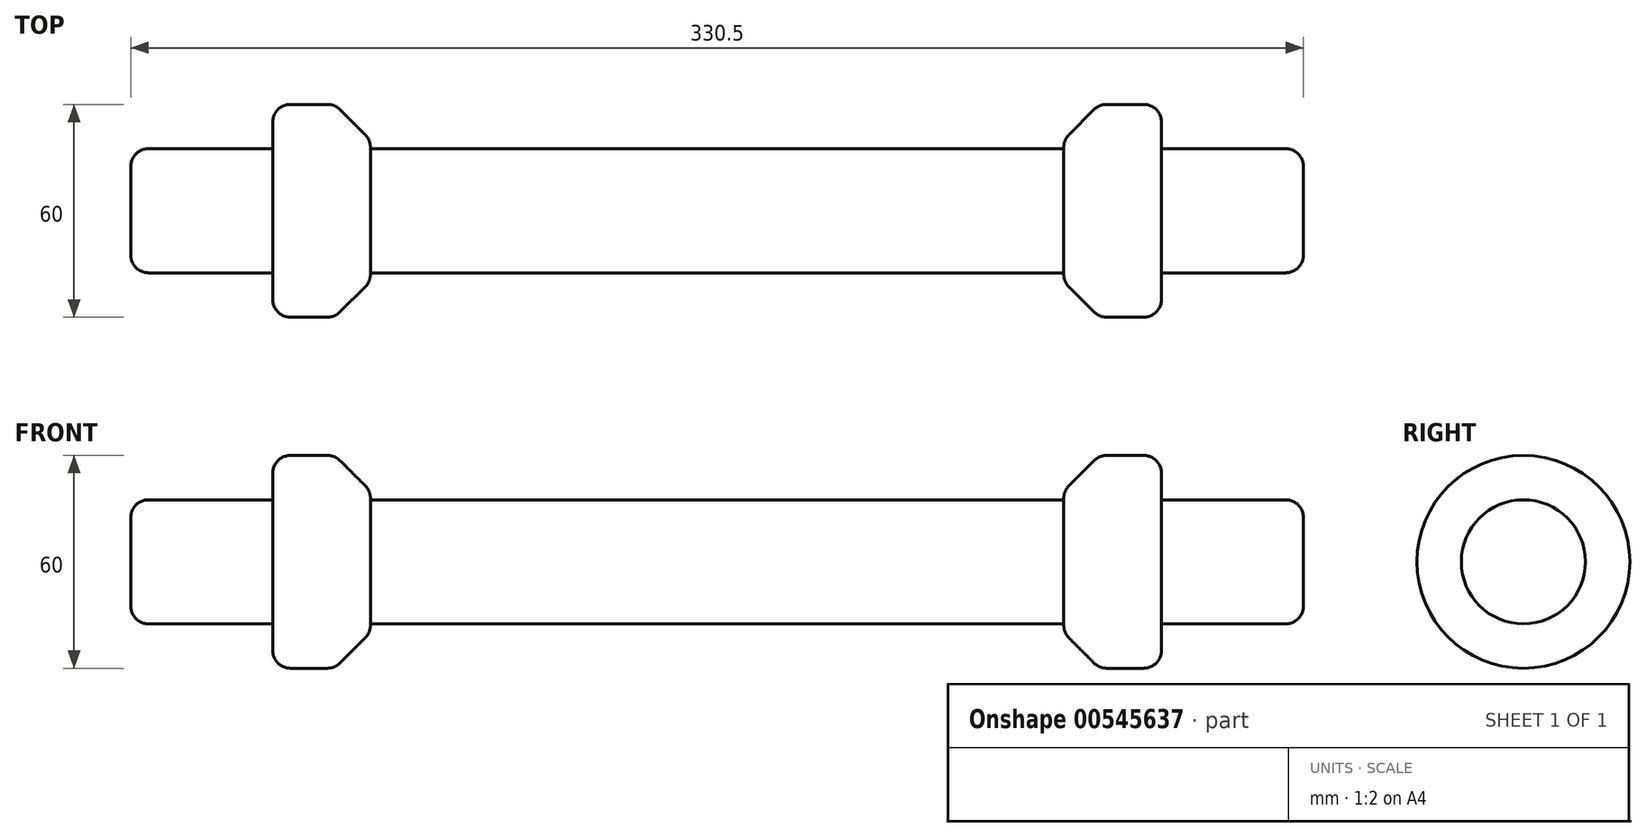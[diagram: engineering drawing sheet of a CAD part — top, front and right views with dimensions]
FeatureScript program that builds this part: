
annotation { "Feature Type Name" : "Feature", "Feature Type Description" : "" }
export const myFeature = defineFeature(function(context is Context, id is Id, definition is map)
    precondition{}
    {
        {
            var Q0;
            Q0=qCreatedBy(makeId("Front.planeOp"),FACE);
            var sketch = newSketch(context, id + "F0", { "sketchPlane" : qUnion([Q0])});
            skLineSegment(sketch, "E0", {"start": v(0, 0) * mm, "end": v(165.25, 0) * mm});
            skLineSegment(sketch, "E1", {"start": v(165.25, 0) * mm, "end": v(165.25, 17.5) * mm});
            skLineSegment(sketch, "E2", {"start": v(165.25, 17.5) * mm, "end": v(125.25, 17.5) * mm});
            skLineSegment(sketch, "E3", {"start": v(125.25, 17.5) * mm, "end": v(125.25, 30) * mm});
            skLineSegment(sketch, "E4", {"start": v(125.25, 30) * mm, "end": v(97.7, 30) * mm});
            skLineSegment(sketch, "E5", {"start": v(97.7, 30) * mm, "end": v(97.7, 17.5) * mm});
            skLineSegment(sketch, "E6", {"start": v(0, 0) * mm, "end": v(0, 17.5) * mm});
            skLineSegment(sketch, "E7", {"start": v(97.7, 17.5) * mm, "end": v(0, 17.5) * mm});
            skSolve(sketch);
        }
        {
            var Q0;
            Q0=makeQuery(id+"F0.imprint","IMPRINT",FACE,{"disambiguationData":[TD([[makeQuery(id+"F0.imprint","IMPRINT",EDGE,{"derivedFrom":sQuery(id+"F0.wireOp",EDGE,"E0")}),1.0]])]});
            var Q1;
            Q1=sQuery(id+"F0.wireOp",EDGE,"E0");
            revolve(context, id + "F1", {"entities" : qUnion([Q0]), "axis" : qUnion([Q1]), "revolveType" : RevolveType.FULL});
        }
        {
            var Q0;
            Q0=makeQuery(id+"F1.opRevolve","SWEPT_BODY",BODY,{"disambiguationData":[OSD([sQuery(id+"F0.wireOp",EDGE,"E0"),sQuery(id+"F0.wireOp",EDGE,"E1"),sQuery(id+"F0.wireOp",EDGE,"E2"),sQuery(id+"F0.wireOp",EDGE,"E3"),sQuery(id+"F0.wireOp",EDGE,"E4"),sQuery(id+"F0.wireOp",EDGE,"E5"),sQuery(id+"F0.wireOp",EDGE,"E6"),sQuery(id+"F0.wireOp",EDGE,"E7")])]});
            var Q1;
            Q1=makeQuery(id+"F1.opRevolve","SWEPT_FACE",FACE,{"disambiguationData":[OSD([sQuery(id+"F0.wireOp",EDGE,"E6")])]});
            mirror(context, id + "F2", {"operationType" : NewBodyOperationType.ADD, "entities" : qUnion([Q0]), "mirrorPlane" : qUnion([Q1])});
        }
        {
            var Q0;
            Q0=makeQuery(id+"F1.opRevolve","SWEPT_EDGE",EDGE,{"disambiguationData":[OSD([sQuery(id+"F0.wireOp",EDGE,"E4"),sQuery(id+"F0.wireOp",EDGE,"E5")])]});
            var Q1;
            Q1=makeQuery(id+"F2.opPattern","COPY",EDGE,{"derivedFrom":makeQuery(id+"F1.opRevolve","SWEPT_EDGE",EDGE,{"disambiguationData":[OSD([sQuery(id+"F0.wireOp",EDGE,"E4"),sQuery(id+"F0.wireOp",EDGE,"E5")])]}),"instanceName":"1"});
            chamfer(context, id + "F3", {"entities" : qUnion([Q0, Q1]), "width" : 10 * mm, "tangentPropagation" : true});
        }
        {
            var Q0;
            {var subQ0=sQuery(id+"F0.wireOp",EDGE,"E4");Q0=makeQuery(id+"F3.opChamfer","BLEND_EDGE",EDGE,{"blendedFrom":[makeQuery(id+"F2.opPattern","COPY",EDGE,{"derivedFrom":makeQuery(id+"F1.opRevolve","SWEPT_EDGE",EDGE,{"disambiguationData":[OSD([subQ0,sQuery(id+"F0.wireOp",EDGE,"E5")])]}),"instanceName":"1"}),makeQuery(id+"F2.opPattern","COPY",FACE,{"derivedFrom":makeQuery(id+"F1.opRevolve","SWEPT_FACE",FACE,{"disambiguationData":[OSD([subQ0])]}),"instanceName":"1"})],"blendedInto":[makeQuery(id+"F2.opPattern","COPY",FACE,{"derivedFrom":makeQuery(id+"F1.opRevolve","SWEPT_FACE",FACE,{"disambiguationData":[OSD([subQ0])]}),"instanceName":"1"})]});}
            var Q1;
            {var subQ0=sQuery(id+"F0.wireOp",EDGE,"E5");Q1=makeQuery(id+"F3.opChamfer","BLEND_EDGE",EDGE,{"blendedFrom":[makeQuery(id+"F2.opPattern","COPY",EDGE,{"derivedFrom":makeQuery(id+"F1.opRevolve","SWEPT_EDGE",EDGE,{"disambiguationData":[OSD([sQuery(id+"F0.wireOp",EDGE,"E4"),subQ0])]}),"instanceName":"1"}),makeQuery(id+"F2.opPattern","COPY",FACE,{"derivedFrom":makeQuery(id+"F1.opRevolve","SWEPT_FACE",FACE,{"disambiguationData":[OSD([subQ0])]}),"instanceName":"1"})],"blendedInto":[makeQuery(id+"F2.opPattern","COPY",FACE,{"derivedFrom":makeQuery(id+"F1.opRevolve","SWEPT_FACE",FACE,{"disambiguationData":[OSD([subQ0])]}),"instanceName":"1"})]});}
            var Q2;
            {var subQ0=sQuery(id+"F0.wireOp",EDGE,"E5");Q2=makeQuery(id+"F3.opChamfer","BLEND_EDGE",EDGE,{"blendedFrom":[makeQuery(id+"F1.opRevolve","SWEPT_EDGE",EDGE,{"disambiguationData":[OSD([sQuery(id+"F0.wireOp",EDGE,"E4"),subQ0])]}),makeQuery(id+"F1.opRevolve","SWEPT_FACE",FACE,{"disambiguationData":[OSD([subQ0])]})],"blendedInto":[makeQuery(id+"F1.opRevolve","SWEPT_FACE",FACE,{"disambiguationData":[OSD([subQ0])]})]});}
            var Q3;
            {var subQ0=sQuery(id+"F0.wireOp",EDGE,"E4");Q3=makeQuery(id+"F3.opChamfer","BLEND_EDGE",EDGE,{"blendedFrom":[makeQuery(id+"F1.opRevolve","SWEPT_EDGE",EDGE,{"disambiguationData":[OSD([subQ0,sQuery(id+"F0.wireOp",EDGE,"E5")])]}),makeQuery(id+"F1.opRevolve","SWEPT_FACE",FACE,{"disambiguationData":[OSD([subQ0])]})],"blendedInto":[makeQuery(id+"F1.opRevolve","SWEPT_FACE",FACE,{"disambiguationData":[OSD([subQ0])]})]});}
            fillet(context, id + "F4", {"entities" : qUnion([Q0, Q1, Q2, Q3]), "radius" : 5 * mm, "tangentPropagation" : true, "allowEdgeOverflow" : false});
        }
        {
            var Q0;
            Q0=makeQuery(id+"F2.opPattern","COPY",FACE,{"derivedFrom":makeQuery(id+"F1.opRevolve","SWEPT_FACE",FACE,{"disambiguationData":[OSD([sQuery(id+"F0.wireOp",EDGE,"E1")])]}),"instanceName":"1"});
            var Q1;
            Q1=makeQuery(id+"F1.opRevolve","SWEPT_EDGE",EDGE,{"disambiguationData":[OSD([sQuery(id+"F0.wireOp",EDGE,"E1"),sQuery(id+"F0.wireOp",EDGE,"E2")])]});
            var Q2;
            Q2=makeQuery(id+"F1.opRevolve","SWEPT_EDGE",EDGE,{"disambiguationData":[OSD([sQuery(id+"F0.wireOp",EDGE,"E3"),sQuery(id+"F0.wireOp",EDGE,"E4")])]});
            var Q3;
            Q3=makeQuery(id+"F2.opPattern","COPY",EDGE,{"derivedFrom":makeQuery(id+"F1.opRevolve","SWEPT_EDGE",EDGE,{"disambiguationData":[OSD([sQuery(id+"F0.wireOp",EDGE,"E3"),sQuery(id+"F0.wireOp",EDGE,"E4")])]}),"instanceName":"1"});
            fillet(context, id + "F5", {"entities" : qUnion([Q0, Q1, Q2, Q3]), "radius" : 5 * mm, "tangentPropagation" : true, "allowEdgeOverflow" : false});
        }
    });
